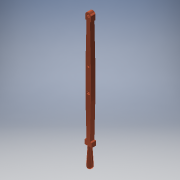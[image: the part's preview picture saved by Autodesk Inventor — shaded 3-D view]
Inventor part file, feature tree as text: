
AUTODESK INVENTOR PART (.ipt)
format: ipt  version: 2017 (Build 210142000, 142)  size: 190,976 bytes
history: native  units: mm
features: sketch x4, extrude x3, plane x1, revolve x1, fillet x1, projected_geometry x1
ambient origin geometry x8: Origin, YZ Plane, XZ Plane, XY Plane, X Axis, Y Axis, Z Axis, Center Point
bodies: Solid1 (feature_tree)
feature tree (11):
  extrude  "Extrusion1"  Depth=3.25mm
  extrude  "Extrusion2"  Depth=5.0mm
  extrude  "Extrusion5"  Depth=4.0mm
  plane  "Work Plane1"
  revolve  "Revolution2"  [1 undecoded]
  fillet  "Fillet1"  Radius=8.0mm
  sketch  "Sketch1"  dims[d0=6.5mm d1=5.0mm d2=6.0mm d3=4.0mm d4=3.5mm d5=90.0deg d6=15.940479mm d7=15.458015mm d8=15.940479mm d9=15.458015mm d10=118.0mm d11=0.25mm d12=6.25mm d13=1.999459mm d14=43.0mm d15=3.25mm d16=78.0mm d17=3.25mm d18=0.0mm d19=3.25mm]
  sketch  "Sketch2"  dims[d20=5.0mm d21=0.0mm d22=2.5mm d23=3.5mm d25=3.5mm d26=50.0mm]
  sketch  "Sketch6"  dims[d27=0.0mm d28=0.0mm d43=4.0mm]
  sketch  "Sketch11"  dims[d44=4.0mm d45=5.0mm d46=8.0mm d47=5.0mm d48=0.0mm d66=0.0mm d67=2.0mm d68=3.25mm d72=2.646694mm d73=30.0mm d76=2.646694mm d78=1.5mm d80=30.916343mm d81=6.636616mm d82=0.541052mm d83=90.0deg d84=3.0mm d107=0.489974mm d109=16.962591mm d110=25.3532mm d111=3.065017mm d112=16.962591mm d113=25.3532mm d114=7.146642mm d116=45.0mm d117=0.0mm d118=76.0mm]
  projected_geometry  "Projected Loop1"
note: 1 required parameter value undecoded (feature->parameter linkage not recoverable at this tier; creation-order binding heuristic only, values carry confidence <= 0.55)
